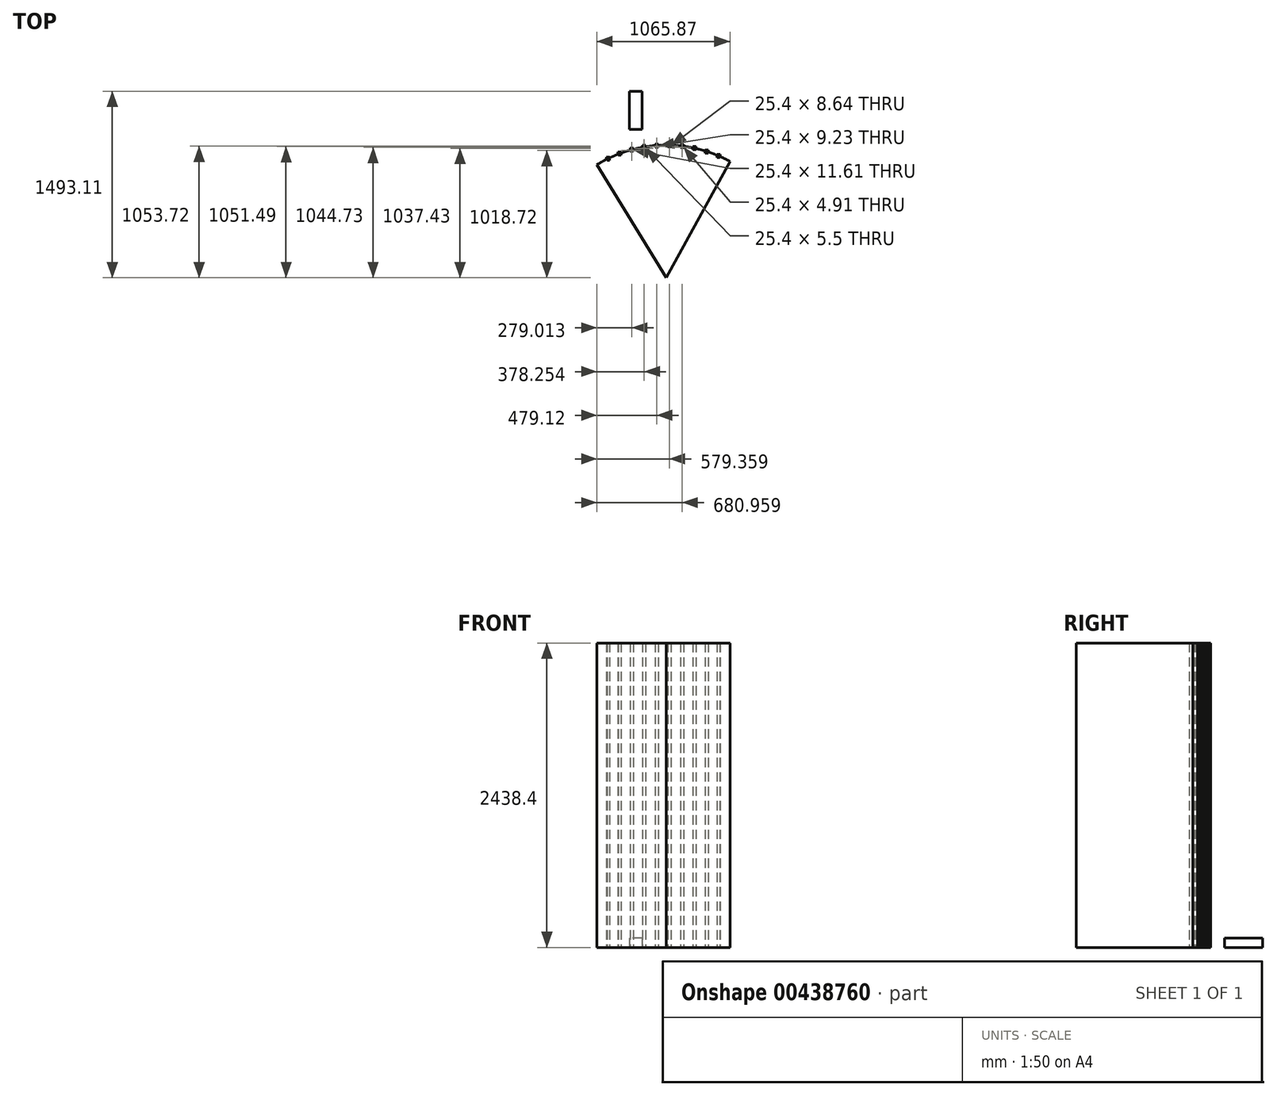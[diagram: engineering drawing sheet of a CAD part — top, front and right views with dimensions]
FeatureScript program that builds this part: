
annotation { "Feature Type Name" : "Feature", "Feature Type Description" : "" }
export const myFeature = defineFeature(function(context is Context, id is Id, definition is map)
    precondition{}
    {
        {
            var Q0;
            Q0=qCreatedBy(makeId("Top.planeOp"),FACE);
            var sketch = newSketch(context, id + "F0", { "sketchPlane" : qUnion([Q0])});
            skArc(sketch, "E0", {"start": v(-555.98, 905.25) * mm, "mid": v(-26.65, 1062.02) * mm, "end": v(509.89, 932) * mm});
            skLineSegment(sketch, "E1", {"start": v(-555.98, 905.25) * mm, "end": v(0, 0) * mm});
            skLineSegment(sketch, "E2", {"start": v(0, 0) * mm, "end": v(509.89, 932) * mm});
            skLineSegment(sketch, "E3", {"start": v(0, 0) * mm, "end": v(-26.65, 1062.02) * mm});
            skLineSegment(sketch, "E4", {"start": v(0, 0) * mm, "end": v(-301.68, 1018.62) * mm});
            skLineSegment(sketch, "E5", {"start": v(-555.98, 905.25) * mm, "end": v(509.89, 932) * mm});
            skPoint(sketch, "E6", {"position": v(-23.05, 918.62) * mm});
            skLineSegment(sketch, "E7", {"start": v(-555.98, 905.25) * mm, "end": v(-301.68, 1018.62) * mm});
            skLineSegment(sketch, "E8", {"start": v(-301.68, 1018.62) * mm, "end": v(-26.65, 1062.02) * mm});
            skPoint(sketch, "E9.end.orphan", {"position": v(-301.68, 911.63) * mm});
            skLineSegment(sketch, "E10", {"start": v(0, 0) * mm, "end": v(250.21, 1032.47) * mm});
            skLineSegment(sketch, "E11", {"start": v(250.21, 1032.47) * mm, "end": v(-26.65, 1062.02) * mm});
            skLineSegment(sketch, "E12", {"start": v(509.89, 932) * mm, "end": v(250.21, 1032.47) * mm});
            skPoint(sketch, "E13", {"position": v(-466.96, 954.22) * mm});
            skPoint(sketch, "E14", {"position": v(418.53, 976.44) * mm});
            skPoint(sketch, "E15", {"position": v(-373.67, 994.47) * mm});
            skPoint(sketch, "E16", {"position": v(323.33, 1011.95) * mm});
            skPoint(sketch, "E17", {"position": v(225.19, 1038.21) * mm});
            skPoint(sketch, "E18", {"position": v(124.98, 1054.98) * mm});
            skPoint(sketch, "E19", {"position": v(23.38, 1062.1) * mm});
            skPoint(sketch, "E20", {"position": v(-276.97, 1025.62) * mm});
            skPoint(sketch, "E21", {"position": v(-177.73, 1047.38) * mm});
            skPoint(sketch, "E22", {"position": v(-76.86, 1059.57) * mm});
            skLineSegment(sketch, "E23.bottom", {"start": v(-454.26, 966.92) * mm, "end": v(-479.66, 966.92) * mm});
            skLineSegment(sketch, "E23.top", {"start": v(-454.26, 941.52) * mm, "end": v(-479.66, 941.52) * mm});
            skLineSegment(sketch, "E23.left", {"start": v(-454.26, 966.92) * mm, "end": v(-454.26, 941.52) * mm});
            skLineSegment(sketch, "E23.right", {"start": v(-479.66, 966.92) * mm, "end": v(-479.66, 941.52) * mm});
            skLineSegment(sketch, "E24.bottom", {"start": v(-360.97, 1007.17) * mm, "end": v(-386.37, 1007.17) * mm});
            skLineSegment(sketch, "E24.top", {"start": v(-360.97, 981.77) * mm, "end": v(-386.37, 981.77) * mm});
            skLineSegment(sketch, "E24.left", {"start": v(-360.97, 1007.17) * mm, "end": v(-360.97, 981.77) * mm});
            skLineSegment(sketch, "E24.right", {"start": v(-386.37, 1007.17) * mm, "end": v(-386.37, 981.77) * mm});
            skLineSegment(sketch, "E25.bottom", {"start": v(-264.27, 1038.32) * mm, "end": v(-289.67, 1038.32) * mm});
            skLineSegment(sketch, "E25.top", {"start": v(-264.27, 1012.92) * mm, "end": v(-289.67, 1012.92) * mm});
            skLineSegment(sketch, "E25.left", {"start": v(-264.27, 1038.32) * mm, "end": v(-264.27, 1012.92) * mm});
            skLineSegment(sketch, "E25.right", {"start": v(-289.67, 1038.32) * mm, "end": v(-289.67, 1012.92) * mm});
            skLineSegment(sketch, "E26.bottom", {"start": v(-165.03, 1060.08) * mm, "end": v(-190.43, 1060.08) * mm});
            skLineSegment(sketch, "E26.top", {"start": v(-165.03, 1034.68) * mm, "end": v(-190.43, 1034.68) * mm});
            skLineSegment(sketch, "E26.left", {"start": v(-165.03, 1060.08) * mm, "end": v(-165.03, 1034.68) * mm});
            skLineSegment(sketch, "E26.right", {"start": v(-190.43, 1060.08) * mm, "end": v(-190.43, 1034.68) * mm});
            skLineSegment(sketch, "E27.bottom", {"start": v(36.08, 1074.8) * mm, "end": v(10.68, 1074.8) * mm});
            skLineSegment(sketch, "E27.top", {"start": v(36.08, 1049.4) * mm, "end": v(10.68, 1049.4) * mm});
            skLineSegment(sketch, "E27.left", {"start": v(36.08, 1074.8) * mm, "end": v(36.08, 1049.4) * mm});
            skLineSegment(sketch, "E27.right", {"start": v(10.68, 1074.8) * mm, "end": v(10.68, 1049.4) * mm});
            skLineSegment(sketch, "E28.bottom", {"start": v(-64.16, 1072.27) * mm, "end": v(-89.56, 1072.27) * mm});
            skLineSegment(sketch, "E28.top", {"start": v(-64.16, 1046.87) * mm, "end": v(-89.56, 1046.87) * mm});
            skLineSegment(sketch, "E28.left", {"start": v(-64.16, 1072.27) * mm, "end": v(-64.16, 1046.87) * mm});
            skLineSegment(sketch, "E28.right", {"start": v(-89.56, 1072.27) * mm, "end": v(-89.56, 1046.87) * mm});
            skLineSegment(sketch, "E29.bottom", {"start": v(137.68, 1067.68) * mm, "end": v(112.28, 1067.68) * mm});
            skLineSegment(sketch, "E29.top", {"start": v(137.68, 1042.28) * mm, "end": v(112.28, 1042.28) * mm});
            skLineSegment(sketch, "E29.left", {"start": v(137.68, 1067.68) * mm, "end": v(137.68, 1042.28) * mm});
            skLineSegment(sketch, "E29.right", {"start": v(112.28, 1067.68) * mm, "end": v(112.28, 1042.28) * mm});
            skLineSegment(sketch, "E30.bottom", {"start": v(212.49, 1050.91) * mm, "end": v(237.89, 1050.91) * mm});
            skLineSegment(sketch, "E30.top", {"start": v(212.49, 1025.51) * mm, "end": v(237.89, 1025.51) * mm});
            skLineSegment(sketch, "E30.left", {"start": v(212.49, 1050.91) * mm, "end": v(212.49, 1025.51) * mm});
            skLineSegment(sketch, "E30.right", {"start": v(237.89, 1050.91) * mm, "end": v(237.89, 1025.51) * mm});
            skLineSegment(sketch, "E31.bottom", {"start": v(336.03, 1024.65) * mm, "end": v(310.63, 1024.65) * mm});
            skLineSegment(sketch, "E31.top", {"start": v(336.03, 999.25) * mm, "end": v(310.63, 999.25) * mm});
            skLineSegment(sketch, "E31.left", {"start": v(336.03, 1024.65) * mm, "end": v(336.03, 999.25) * mm});
            skLineSegment(sketch, "E31.right", {"start": v(310.63, 1024.65) * mm, "end": v(310.63, 999.25) * mm});
            skLineSegment(sketch, "E32.bottom", {"start": v(405.83, 989.14) * mm, "end": v(431.23, 989.14) * mm});
            skLineSegment(sketch, "E32.top", {"start": v(405.83, 963.74) * mm, "end": v(431.23, 963.74) * mm});
            skLineSegment(sketch, "E32.left", {"start": v(405.83, 989.14) * mm, "end": v(405.83, 963.74) * mm});
            skLineSegment(sketch, "E32.right", {"start": v(431.23, 989.14) * mm, "end": v(431.23, 963.74) * mm});
            skSolve(sketch);
        }
        {
            var Q0;
            {var subQ0=sQuery(id+"F0.wireOp",EDGE,"E2");Q0=makeQuery(id+"F0.imprint","IMPRINT",FACE,{"disambiguationData":[TD([[makeQuery(id+"F0.imprint","IMPRINT",EDGE,{"derivedFrom":subQ0}),1.0]])]});}
            var Q1;
            {var subQ0=sQuery(id+"F0.wireOp",EDGE,"E1");Q1=makeQuery(id+"F0.imprint","IMPRINT",FACE,{"disambiguationData":[TD([[makeQuery(id+"F0.imprint","IMPRINT",EDGE,{"derivedFrom":subQ0}),1.0]])]});}
            var Q2;
            Q2 = qSketchRegion(id + "F0", true);
            extrude(context, id + "F1", {"entities" : qUnion([Q0, Q1, Q2]), "depth" : 2438.4 * mm});
        }
        {
            var Q0;
            Q0=qCreatedBy(makeId("Top.planeOp"),FACE);
            var sketch = newSketch(context, id + "F2", { "sketchPlane" : qUnion([Q0])});
            skLineSegment(sketch, "E33.bottom", {"start": v(-195.02, 1188.3) * mm, "end": v(-296.62, 1188.3) * mm});
            skLineSegment(sketch, "E33.top", {"start": v(-195.02, 1493.1) * mm, "end": v(-296.62, 1493.1) * mm});
            skLineSegment(sketch, "E33.left", {"start": v(-195.02, 1188.3) * mm, "end": v(-195.02, 1493.1) * mm});
            skLineSegment(sketch, "E33.right", {"start": v(-296.62, 1188.3) * mm, "end": v(-296.62, 1493.1) * mm});
            skSolve(sketch);
        }
        {
            var Q0;
            Q0 = qSketchRegion(id + "F2", true);
            extrude(context, id + "F3", {"entities" : qUnion([Q0]), "depth" : 76.2 * mm});
        }
    });
